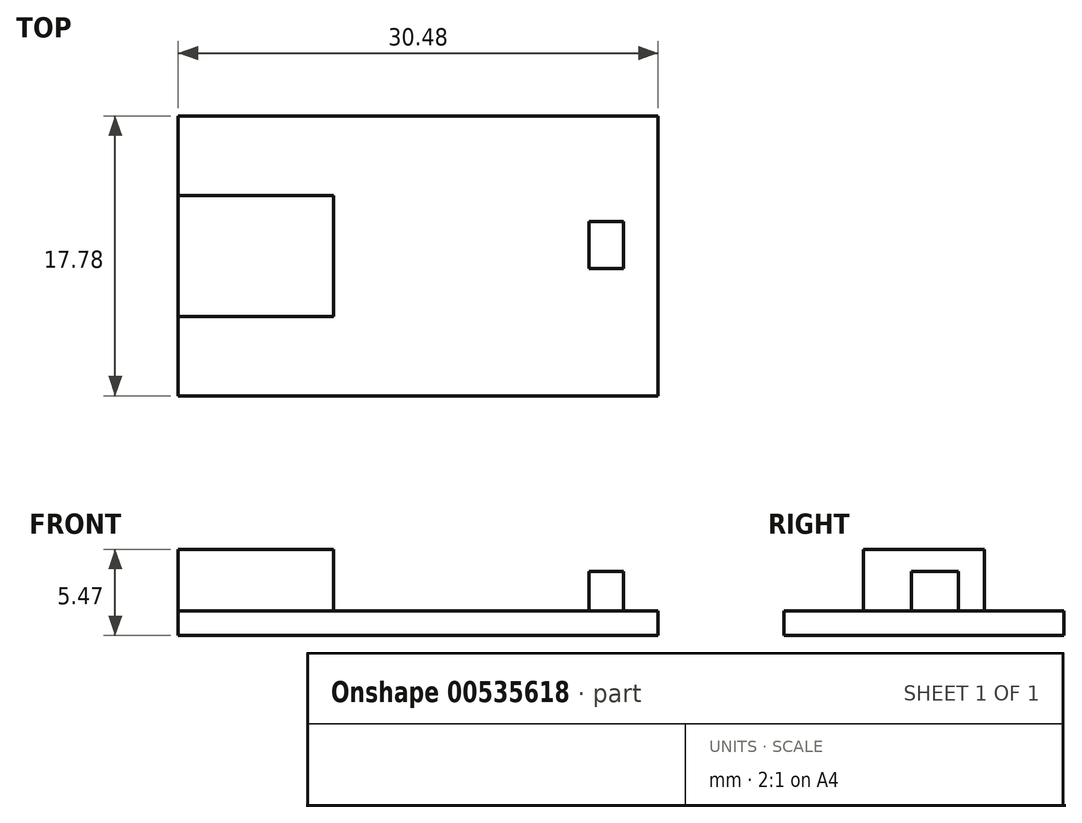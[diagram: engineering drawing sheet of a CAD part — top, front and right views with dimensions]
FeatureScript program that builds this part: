
annotation { "Feature Type Name" : "Feature", "Feature Type Description" : "" }
export const myFeature = defineFeature(function(context is Context, id is Id, definition is map)
    precondition{}
    {
        {
            var Q0;
            Q0=qCreatedBy(makeId("Top.planeOp"),FACE);
            var sketch = newSketch(context, id + "F0", { "sketchPlane" : qUnion([Q0])});
            skLineSegment(sketch, "E0.bottom", {"start": v(15.24, 8.89) * mm, "end": v(-15.24, 8.89) * mm});
            skLineSegment(sketch, "E0.top", {"start": v(15.24, -8.9) * mm, "end": v(-15.24, -8.9) * mm});
            skLineSegment(sketch, "E0.left", {"start": v(15.24, 8.89) * mm, "end": v(15.24, -8.9) * mm});
            skLineSegment(sketch, "E0.right", {"start": v(-15.24, 8.89) * mm, "end": v(-15.24, -8.9) * mm});
            skPoint(sketch, "E0.middle", {"position": v(0, 0) * mm});
            skSolve(sketch);
        }
        {
            var Q0;
            Q0=makeQuery(id+"F0.imprint","IMPRINT",FACE,{"disambiguationData":[TD([[makeQuery(id+"F0.imprint","IMPRINT",EDGE,{"derivedFrom":sQuery(id+"F0.wireOp",EDGE,"E0.bottom")}),1.0]])]});
            extrude(context, id + "F1", {"entities" : qUnion([Q0]), "depth" : 1.57 * mm, "offsetDistance" : 25 * mm});
        }
        {
            var Q0;
            Q0=makeQuery(id+"F1.opExtrude","CAP_FACE",FACE,{"disambiguationData":[OSD([sQuery(id+"F0.wireOp",EDGE,"E0.bottom"),sQuery(id+"F0.wireOp",EDGE,"E0.top"),sQuery(id+"F0.wireOp",EDGE,"E0.left"),sQuery(id+"F0.wireOp",EDGE,"E0.right")])],"isStart":false});
            var sketch = newSketch(context, id + "F2", { "sketchPlane" : qUnion([Q0])});
            skLineSegment(sketch, "E1.bottom", {"start": v(-15.24, 3.85) * mm, "end": v(-5.4, 3.85) * mm});
            skLineSegment(sketch, "E1.top", {"start": v(-15.24, -3.85) * mm, "end": v(-5.4, -3.85) * mm});
            skLineSegment(sketch, "E1.left", {"start": v(-15.24, 3.85) * mm, "end": v(-15.24, -3.85) * mm});
            skLineSegment(sketch, "E1.right", {"start": v(-5.4, 3.85) * mm, "end": v(-5.4, -3.85) * mm});
            skSolve(sketch);
        }
        {
            var Q0;
            Q0=makeQuery(id+"F2.imprint","IMPRINT",FACE,{"disambiguationData":[TD([[makeQuery(id+"F2.imprint","IMPRINT",EDGE,{"derivedFrom":sQuery(id+"F2.wireOp",EDGE,"E1.bottom")}),-1.0]])]});
            extrude(context, id + "F3", {"entities" : qUnion([Q0]), "operationType" : NewBodyOperationType.ADD, "depth" : 3.9 * mm, "offsetDistance" : 25 * mm});
        }
        {
            var Q0;
            Q0=makeQuery(id+"F1.opExtrude","CAP_FACE",FACE,{"disambiguationData":[OSD([sQuery(id+"F0.wireOp",EDGE,"E0.bottom"),sQuery(id+"F0.wireOp",EDGE,"E0.top"),sQuery(id+"F0.wireOp",EDGE,"E0.left"),sQuery(id+"F0.wireOp",EDGE,"E0.right")])],"isStart":false});
            var sketch = newSketch(context, id + "F4", { "sketchPlane" : qUnion([Q0])});
            skLineSegment(sketch, "E2.bottom", {"start": v(13.04, 2.19) * mm, "end": v(10.84, 2.19) * mm});
            skLineSegment(sketch, "E2.top", {"start": v(13.04, -0.81) * mm, "end": v(10.84, -0.81) * mm});
            skLineSegment(sketch, "E2.left", {"start": v(13.04, 2.19) * mm, "end": v(13.04, -0.81) * mm});
            skLineSegment(sketch, "E2.right", {"start": v(10.84, 2.19) * mm, "end": v(10.84, -0.81) * mm});
            skLineSegment(sketch, "E3.0.0", {"start": v(-15.24, 8.89) * mm, "end": v(-15.24, 3.85) * mm});
            skLineSegment(sketch, "E3.0.1", {"start": v(-15.24, 3.85) * mm, "end": v(-5.4, 3.85) * mm});
            skLineSegment(sketch, "E3.0.2", {"start": v(-5.4, 3.85) * mm, "end": v(-5.4, -3.85) * mm});
            skLineSegment(sketch, "E3.0.3", {"start": v(-5.4, -3.85) * mm, "end": v(-15.24, -3.85) * mm});
            skLineSegment(sketch, "E3.0.4", {"start": v(-15.24, -3.85) * mm, "end": v(-15.24, -8.9) * mm});
            skLineSegment(sketch, "E3.0.5", {"start": v(-15.24, -8.9) * mm, "end": v(15.24, -8.9) * mm});
            skLineSegment(sketch, "E3.0.6", {"start": v(15.24, -8.9) * mm, "end": v(15.24, 8.89) * mm});
            skLineSegment(sketch, "E3.0.7", {"start": v(15.24, 8.89) * mm, "end": v(-15.24, 8.89) * mm});
            skLineSegment(sketch, "E4.0.2", {"start": v(15.24, 8.89) * mm, "end": v(15.24, -8.9) * mm});
            skSolve(sketch);
        }
        {
            var Q0;
            Q0=makeQuery(id+"F4.imprint","IMPRINT",FACE,{"disambiguationData":[TD([[makeQuery(id+"F4.imprint","IMPRINT",EDGE,{"derivedFrom":sQuery(id+"F4.wireOp",EDGE,"E2.bottom")}),1.0]])]});
            extrude(context, id + "F5", {"entities" : qUnion([Q0]), "operationType" : NewBodyOperationType.ADD, "depth" : 2.5 * mm, "offsetDistance" : 25 * mm});
        }
    });
